# Revit family: IS_UltraFlat_K5190_BIM_DE
name_source: partatom
category: Plumbing Fixtures
revit_build: Autodesk Revit MEP 2016 (Build: 20161004_0715(x64)
units: mm (PartAtom-declared; Revit-internal decimal feet)

## family parameters
Cut with Voids When Loaded = Yes
Host = Face
OmniClass Number = 23.45.05.14.21.11
OmniClass Title = Bath/Shower Units
Part Type = Normal
Room Calculation Point = No
Round Connector Dimension = Use Diameter
Shared = No

## types (2) — shared parameters
Accessories = www.idealstandard.de\ersatzteile
AreaUnits = millimeters
Assembly Code = C1030200
AssetType = Fixed
Brand = Ideal Standard
CodePerformance = DIN EN 14527, DIN EN 249
Color = White
ConnectionType = Plumbing
CurrencyUnit = €
Description = ULTRA FLAT rectangular shower tray 1700x900mm
DurationUnit = year
ExpectedLife = 25
Features = ULTRA FLAT rectangular shower tray 1700x900mm
Finish = White
GrossWeight = 39 kg
InstallationDate = 1900-12-31T23:59:59
InstallationInstructions = www.idealstandard.de\produkte
LinearUnits = millimeters
ManufacturerURL = www.idealstandard.de
Material = Sanitary Brass
NominalHeight = 40 mm
NominalLength = 900 mm
NominalWidth = 1700 mm
Product data URL = http://bimobject.com
ProductInformation = www.idealstandard.de
Shape = Rectangular
Size = 1700 x 900 x 40 mm
Space = Internal
URL = www.idealstandard.de
Uniclass2015Code = Pr_40_20_06_84
Uniclass2015Title = Shower trays
Uniclass2015Version = Products v1.1
Version = 1
VolumeUnits = Litres
zero-valued in all types: CWFU, Cost, Default Elevation, HWFU, NominalDepth, WFU

## per-type parameters (varying)
| type | BIMObjectName | BarCode | Model | ModelNumber | ModelReference | Name |
| K519001 - ULTRA FLAT rectangular shower tray 1700x900mm | ISI_IdealStandard_Showers_ULTRA FLAT_K519001 | 4015413013451 | K519001 | K519001 | IS Rechteck-Brausewanne ULTRA FLAT, 1700x900x47mm, Weiß | ISI_IdealStandard_Showers_ULTRA FLAT_K519001 |
| K5190YK - ULTRA FLAT rectangular shower tray 1700x900mm | ISI_IdealStandard_Showers_ULTRA FLAT_K5190YK | 4015413036498 | K5190YK | K5190YK | IS Rechteck-Brausewanne ULTRA FLAT, 1700x900x47mm, Weiß mit Ideal Grip | ISI_IdealStandard_Showers_ULTRA FLAT_K5190YK |

## geometry (parser evidence)
native form markers: Blend x4, Sweep x1
no freeform markers — native parametric forms only
